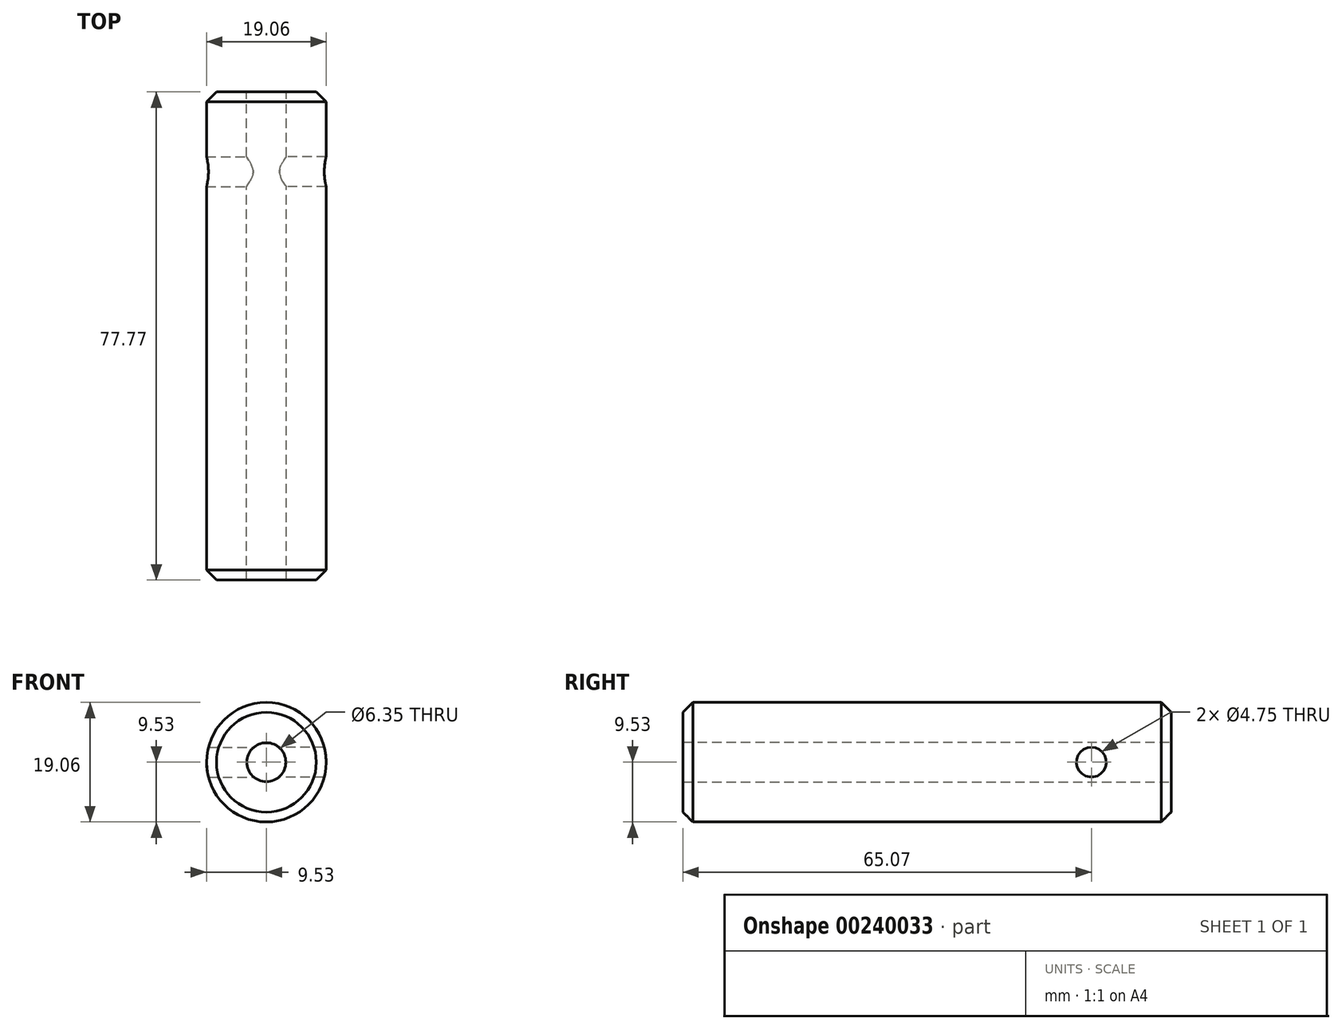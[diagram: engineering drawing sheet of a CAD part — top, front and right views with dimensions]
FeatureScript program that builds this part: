
annotation { "Feature Type Name" : "Feature", "Feature Type Description" : "" }
export const myFeature = defineFeature(function(context is Context, id is Id, definition is map)
    precondition{}
    {
        {
            var Q0;
            Q0=qCreatedBy(makeId("Front.planeOp"),FACE);
            var sketch = newSketch(context, id + "F0", { "sketchPlane" : qUnion([Q0])});
            skCircle(sketch, "E0", {"center": v(0, 0) * mm, "radius": 9.53 * mm});
            skSolve(sketch);
        }
        {
            var Q0;
            Q0 = qSketchRegion(id + "F0", true);
            extrude(context, id + "F1", {"entities" : qUnion([Q0]), "depth" : 77.77 * mm});
        }
        {
            var Q0;
            Q0=qCreatedBy(makeId("Front.planeOp"),FACE);
            var sketch = newSketch(context, id + "F2", { "sketchPlane" : qUnion([Q0])});
            skCircle(sketch, "E1", {"center": v(0, 0) * mm, "radius": 3.18 * mm});
            skSolve(sketch);
        }
        {
            var Q0;
            Q0=sQuery(id+"F2.wireOp",VERTEX,"E1.center");
            var Q1;
            Q1=makeQuery(id+"F1.opExtrude","SWEPT_BODY",BODY,{"disambiguationData":[OSD([sQuery(id+"F0.wireOp",EDGE,"E0")])]});
            hole(context, id + "F3", {"style" : HoleStyle.SIMPLE, "endStyle" : HoleEndStyle.BLIND, "oppositeDirection" : true, "holeDiameter" : 6.35 * mm, "holeDepth" : 77.73 * mm, "locations" : qUnion([Q0]), "scope" : qUnion([Q1])});
        }
        {
            var Q0;
            Q0=makeQuery(id+"F1.opExtrude","CAP_EDGE",EDGE,{"disambiguationData":[OSD([sQuery(id+"F0.wireOp",EDGE,"E0")])],"isStart":false});
            var Q1;
            Q1=makeQuery(id+"F1.opExtrude","CAP_EDGE",EDGE,{"disambiguationData":[OSD([sQuery(id+"F0.wireOp",EDGE,"E0")])],"isStart":true});
            chamfer(context, id + "F4", {"entities" : qUnion([Q0, Q1]), "chamferType" : ChamferType.OFFSET_ANGLE, "width" : 1.57 * mm, "oppositeDirection" : false, "angle" : 45 * degree, "tangentPropagation" : true});
        }
        {
            var Q0;
            Q0=qCreatedBy(makeId("Right.planeOp"),FACE);
            var sketch = newSketch(context, id + "F5", { "sketchPlane" : qUnion([Q0])});
            skCircle(sketch, "E2", {"center": v(-12.7, 0) * mm, "radius": 2.37 * mm});
            skSolve(sketch);
        }
        {
            var Q0;
            Q0=sQuery(id+"F5.wireOp",VERTEX,"E2.center");
            var Q1;
            Q1=makeQuery(id+"F1.opExtrude","SWEPT_BODY",BODY,{"disambiguationData":[OSD([sQuery(id+"F0.wireOp",EDGE,"E0")])]});
            hole(context, id + "F6", {"style" : HoleStyle.SIMPLE, "endStyle" : HoleEndStyle.BLIND, "holeDiameter" : 4.75 * mm, "holeDepth" : 19.05 * mm, "locations" : qUnion([Q0]), "scope" : qUnion([Q1])});
        }
        {
            var Q0;
            Q0=qCreatedBy(makeId("Right.planeOp"),FACE);
            var sketch = newSketch(context, id + "F7", { "sketchPlane" : qUnion([Q0])});
            skCircle(sketch, "E3", {"center": v(-12.7, 0) * mm, "radius": 2.37 * mm});
            skSolve(sketch);
        }
        {
            var Q0;
            Q0=sQuery(id+"F7.wireOp",VERTEX,"E3.center");
            var Q1;
            Q1=makeQuery(id+"F1.opExtrude","SWEPT_BODY",BODY,{"disambiguationData":[OSD([sQuery(id+"F0.wireOp",EDGE,"E0")])]});
            hole(context, id + "F8", {"style" : HoleStyle.SIMPLE, "endStyle" : HoleEndStyle.BLIND, "oppositeDirection" : true, "holeDiameter" : 4.75 * mm, "holeDepth" : 19.05 * mm, "locations" : qUnion([Q0]), "scope" : qUnion([Q1])});
        }
    });
